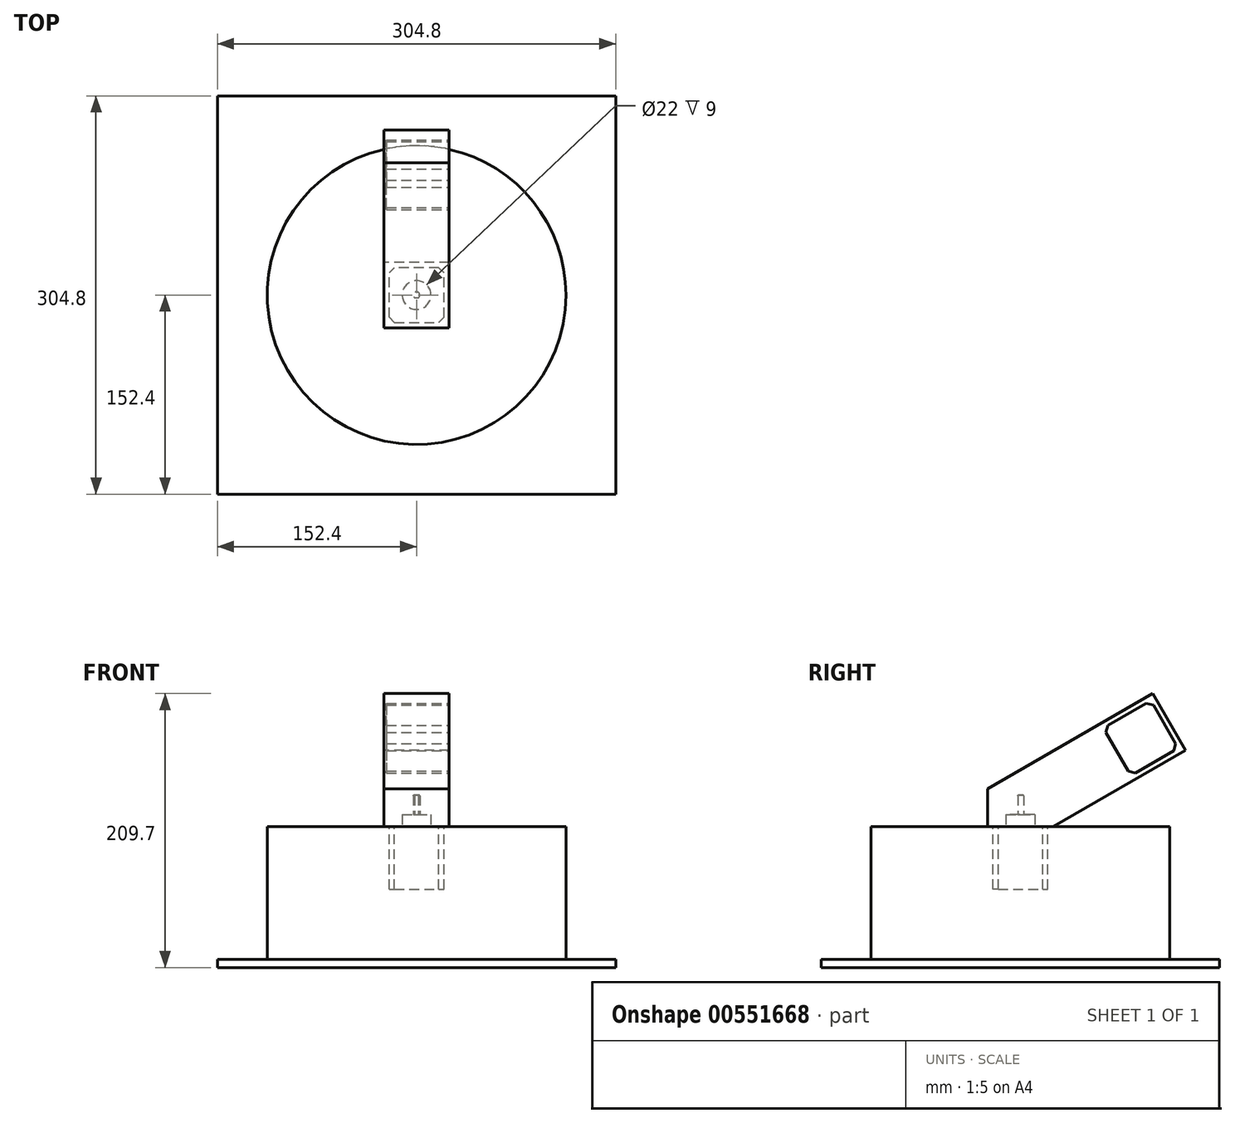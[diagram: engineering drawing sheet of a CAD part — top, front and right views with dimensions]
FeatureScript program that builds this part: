
annotation { "Feature Type Name" : "Feature", "Feature Type Description" : "" }
export const myFeature = defineFeature(function(context is Context, id is Id, definition is map)
    precondition{}
    {
        {
            var Q0;
            Q0=qCreatedBy(makeId("Top.planeOp"),FACE);
            var sketch = newSketch(context, id + "F0", { "sketchPlane" : qUnion([Q0])});
            skLineSegment(sketch, "E0.bottom", {"start": v(152.4, -152.4) * mm, "end": v(-152.4, -152.4) * mm});
            skLineSegment(sketch, "E0.top", {"start": v(152.4, 152.4) * mm, "end": v(-152.4, 152.4) * mm});
            skLineSegment(sketch, "E0.left", {"start": v(152.4, -152.4) * mm, "end": v(152.4, 152.4) * mm});
            skLineSegment(sketch, "E0.right", {"start": v(-152.4, -152.4) * mm, "end": v(-152.4, 152.4) * mm});
            skPoint(sketch, "E0.middle", {"position": v(0, 0) * mm});
            skSolve(sketch);
        }
        {
            var Q0;
            Q0=qSketchRegion(id+"F0",true);
            extrude(context, id + "F1", {"entities" : qUnion([Q0]), "depth" : 6.35 * mm, "offsetDistance" : 25 * mm});
        }
        {
            var Q0;
            Q0=makeQuery(id+"F1.opExtrude","CAP_FACE",FACE,{"disambiguationData":[OSD([sQuery(id+"F0.wireOp",EDGE,"E0.bottom"),sQuery(id+"F0.wireOp",EDGE,"E0.top"),sQuery(id+"F0.wireOp",EDGE,"E0.left"),sQuery(id+"F0.wireOp",EDGE,"E0.right")])],"isStart":false});
            var sketch = newSketch(context, id + "F2", { "sketchPlane" : qUnion([Q0])});
            skCircle(sketch, "E1", {"center": v(0, 0) * mm, "radius": 114.3 * mm});
            skSolve(sketch);
        }
        {
            var Q0;
            Q0=qSketchRegion(id+"F2",true);
            extrude(context, id + "F3", {"entities" : qUnion([Q0]), "operationType" : NewBodyOperationType.ADD, "depth" : 101.6 * mm, "offsetDistance" : 25 * mm});
        }
        {
            var Q0;
            Q0=makeQuery(id+"F3.opExtrude","CAP_FACE",FACE,{"disambiguationData":[OSD([sQuery(id+"F2.wireOp",EDGE,"E1")])],"isStart":false});
            var sketch = newSketch(context, id + "F4", { "sketchPlane" : qUnion([Q0])});
            skLineSegment(sketch, "E2.bottom", {"start": v(25, -25) * mm, "end": v(-25, -25) * mm});
            skLineSegment(sketch, "E2.top", {"start": v(25, 25) * mm, "end": v(-25, 25) * mm});
            skLineSegment(sketch, "E2.left", {"start": v(25, -25) * mm, "end": v(25, 25) * mm});
            skLineSegment(sketch, "E2.right", {"start": v(-25, -25) * mm, "end": v(-25, 25) * mm});
            skPoint(sketch, "E2.middle", {"position": v(0, 0) * mm});
            skSolve(sketch);
        }
        {
            var Q0;
            Q0=qSketchRegion(id+"F4",true);
            extrude(context, id + "F5", {"entities" : qUnion([Q0]), "depth" : 28.87 * mm, "offsetDistance" : 25 * mm});
        }
        {
            var Q0;
            Q0=makeQuery(id+"F5.opExtrude","SWEPT_FACE",FACE,{"disambiguationData":[OSD([sQuery(id+"F4.wireOp",EDGE,"E2.right")])]});
            var sketch = newSketch(context, id + "F6", { "sketchPlane" : qUnion([Q0])});
            skLineSegment(sketch, "E3", {"start": v(25, 136.82) * mm, "end": v(-101.24, 209.7) * mm});
            skLineSegment(sketch, "E4", {"start": v(-25, 107.95) * mm, "end": v(-126.24, 166.4) * mm});
            skLineSegment(sketch, "E5", {"start": v(-126.24, 166.4) * mm, "end": v(-101.24, 209.7) * mm});
            skSolve(sketch);
        }
        {
            var Q0;
            Q0=makeQuery(id+"F6.imprint","IMPRINT",FACE,{"disambiguationData":[TD([[makeQuery(id+"F6.imprint","IMPRINT",EDGE,{"derivedFrom":sQuery(id+"F6.wireOp",EDGE,"E3")}),1.0]])]});
            extrude(context, id + "F7", {"entities" : qUnion([Q0]), "operationType" : NewBodyOperationType.ADD, "oppositeDirection" : true, "depth" : 50 * mm, "offsetDistance" : 25 * mm});
        }
        {
            var Q0;
            Q0=makeQuery(id+"F7.boolean.opBoolean","MERGE",FACE,{"derivedFrom":[makeQuery(id+"F5.opExtrude","SWEPT_FACE",FACE,{"disambiguationData":[OSD([sQuery(id+"F4.wireOp",EDGE,"E2.left")])]}),makeQuery(id+"F7.opExtrude","CAP_FACE",FACE,{"disambiguationData":[OSD([sQuery(id+"F4.wireOp",EDGE,"E2.top"),sQuery(id+"F4.wireOp",EDGE,"E2.right"),sQuery(id+"F6.wireOp",EDGE,"E3"),sQuery(id+"F6.wireOp",EDGE,"E4"),sQuery(id+"F6.wireOp",EDGE,"E5")])],"isStart":false})]});
            var sketch = newSketch(context, id + "F8", { "sketchPlane" : qUnion([Q0])});
            skLineSegment(sketch, "E6", {"start": v(66.87, 185.24) * mm, "end": v(96.31, 202.24) * mm});
            skLineSegment(sketch, "E7", {"start": v(96.31, 202.24) * mm, "end": v(101.78, 200.77) * mm});
            skLineSegment(sketch, "E8", {"start": v(101.78, 200.77) * mm, "end": v(118.78, 171.33) * mm});
            skLineSegment(sketch, "E9", {"start": v(118.78, 171.33) * mm, "end": v(117.31, 165.87) * mm});
            skLineSegment(sketch, "E10", {"start": v(117.31, 165.87) * mm, "end": v(87.87, 148.87) * mm});
            skLineSegment(sketch, "E11", {"start": v(87.87, 148.87) * mm, "end": v(82.4, 150.33) * mm});
            skLineSegment(sketch, "E12", {"start": v(66.87, 185.24) * mm, "end": v(65.4, 179.77) * mm});
            skLineSegment(sketch, "E13", {"start": v(65.4, 179.77) * mm, "end": v(82.4, 150.33) * mm});
            skLineSegment(sketch, "E14", {"start": v(76.2, 195.25) * mm, "end": v(78.2, 191.79) * mm, "construction": true});
            skLineSegment(sketch, "E15", {"start": v(99.92, 151.2) * mm, "end": v(97.92, 154.67) * mm, "construction": true});
            skLineSegment(sketch, "E16", {"start": v(110.28, 186.05) * mm, "end": v(113.74, 188.05) * mm, "construction": true});
            skSolve(sketch);
        }
        {
            var Q0;
            Q0=qSketchRegion(id+"F8",true);
            extrude(context, id + "F9", {"entities" : qUnion([Q0]), "operationType" : NewBodyOperationType.REMOVE, "oppositeDirection" : true, "depth" : 48 * mm, "offsetDistance" : 25 * mm});
        }
        {
            var Q0;
            Q0=makeQuery(id+"F3.opExtrude","CAP_FACE",FACE,{"disambiguationData":[OSD([sQuery(id+"F2.wireOp",EDGE,"E1")])],"isStart":false});
            var sketch = newSketch(context, id + "F10", { "sketchPlane" : qUnion([Q0])});
            skPoint(sketch, "E17.middle", {"position": v(0, 0) * mm});
            skLineSegment(sketch, "E18", {"start": v(-21, -17) * mm, "end": v(-17, -21) * mm});
            skLineSegment(sketch, "E19", {"start": v(-21, -17) * mm, "end": v(-21, 17) * mm});
            skLineSegment(sketch, "E20", {"start": v(-21, 17) * mm, "end": v(-17, 21) * mm});
            skLineSegment(sketch, "E21", {"start": v(-17, -21) * mm, "end": v(17, -21) * mm});
            skLineSegment(sketch, "E22", {"start": v(17, -21) * mm, "end": v(21, -17) * mm});
            skLineSegment(sketch, "E23", {"start": v(21, -17) * mm, "end": v(21, 17) * mm});
            skLineSegment(sketch, "E24", {"start": v(21, 17) * mm, "end": v(17, 21) * mm});
            skLineSegment(sketch, "E25", {"start": v(17, 21) * mm, "end": v(-17, 21) * mm});
            skLineSegment(sketch, "E26", {"start": v(0, 0) * mm, "end": v(21, 0) * mm, "construction": true});
            skLineSegment(sketch, "E27", {"start": v(0, 0) * mm, "end": v(0, 21) * mm, "construction": true});
            skLineSegment(sketch, "E28", {"start": v(0, 0) * mm, "end": v(0, -21) * mm, "construction": true});
            skLineSegment(sketch, "E29", {"start": v(0, 0) * mm, "end": v(-21, 0) * mm, "construction": true});
            skSolve(sketch);
        }
        {
            var Q0;
            Q0=qSketchRegion(id+"F10",true);
            extrude(context, id + "F11", {"entities" : qUnion([Q0]), "operationType" : NewBodyOperationType.REMOVE, "oppositeDirection" : true, "depth" : 48 * mm, "offsetDistance" : 25 * mm});
        }
        {
            var Q0;
            Q0=makeQuery(id+"F5.opExtrude","CAP_FACE",FACE,{"disambiguationData":[OSD([sQuery(id+"F4.wireOp",EDGE,"E2.bottom"),sQuery(id+"F4.wireOp",EDGE,"E2.top"),sQuery(id+"F4.wireOp",EDGE,"E2.left"),sQuery(id+"F4.wireOp",EDGE,"E2.right")])],"isStart":true});
            var sketch = newSketch(context, id + "F12", { "sketchPlane" : qUnion([Q0])});
            skCircle(sketch, "E30", {"center": v(0, 0) * mm, "radius": 11 * mm});
            skSolve(sketch);
        }
        {
            var Q0;
            Q0=qSketchRegion(id+"F12",true);
            extrude(context, id + "F13", {"entities" : qUnion([Q0]), "operationType" : NewBodyOperationType.REMOVE, "oppositeDirection" : true, "depth" : 9 * mm, "offsetDistance" : 25 * mm});
        }
        {
            var Q0;
            Q0=makeQuery(id+"F13.boolean.opBoolean","COPY",FACE,{"derivedFrom":makeQuery(id+"F13.opExtrude","CAP_FACE",FACE,{"disambiguationData":[OSD([sQuery(id+"F12.wireOp",EDGE,"E30")])],"isStart":false})});
            var sketch = newSketch(context, id + "F14", { "sketchPlane" : qUnion([Q0])});
            skArc(sketch, "E31", {"start": v(-1.5, 2) * mm, "mid": v(0, -2.5) * mm, "end": v(1.5, 2) * mm});
            skLineSegment(sketch, "E32", {"start": v(-1.5, 2) * mm, "end": v(1.5, 2) * mm});
            skSolve(sketch);
        }
        {
            var Q0;
            Q0=makeQuery(id+"F14.imprint","IMPRINT",FACE,{"disambiguationData":[TD([[makeQuery(id+"F14.imprint","IMPRINT",EDGE,{"derivedFrom":sQuery(id+"F14.wireOp",EDGE,"E31")}),1.0]])]});
            extrude(context, id + "F15", {"entities" : qUnion([Q0]), "operationType" : NewBodyOperationType.REMOVE, "oppositeDirection" : true, "depth" : 15 * mm, "offsetDistance" : 25 * mm});
        }
        {
            var Q0;
            Q0=makeQuery(id+"F15.boolean.opBoolean","COPY",EDGE,{"derivedFrom":makeQuery(id+"F15.opExtrude","CAP_EDGE",EDGE,{"disambiguationData":[OSD([sQuery(id+"F14.wireOp",EDGE,"E31")])],"isStart":false})});
            fillet(context, id + "F16", {"entities" : qUnion([Q0]), "radius" : .5 * mm, "tangentPropagation" : true, "allowEdgeOverflow" : false});
        }
    });
